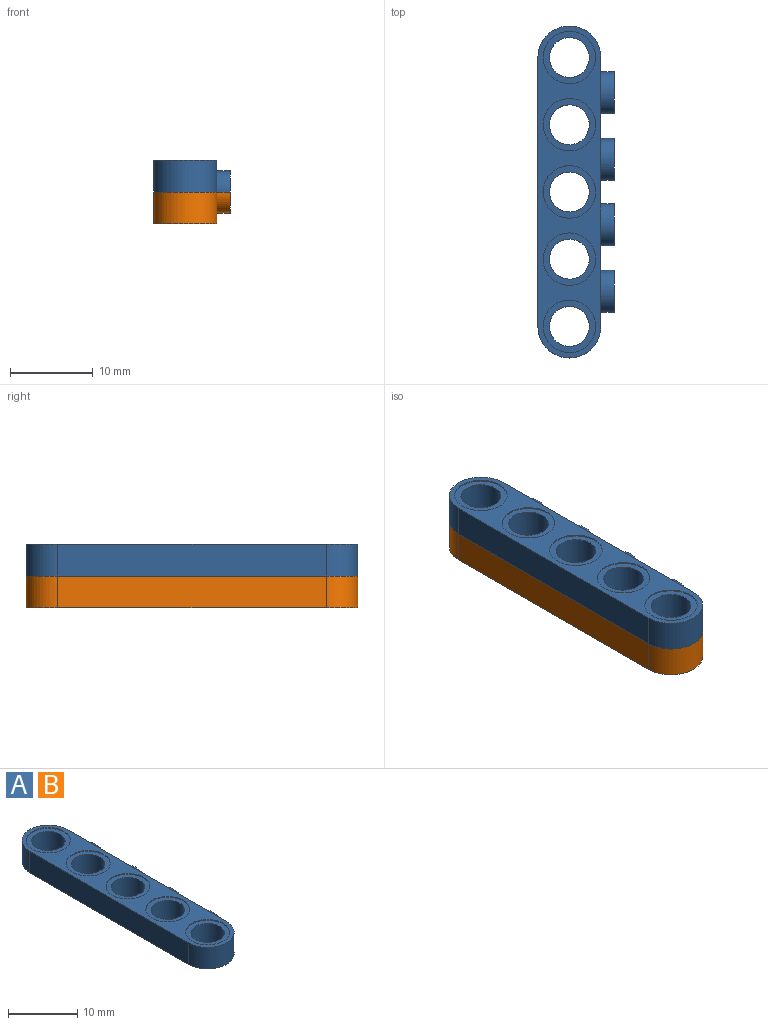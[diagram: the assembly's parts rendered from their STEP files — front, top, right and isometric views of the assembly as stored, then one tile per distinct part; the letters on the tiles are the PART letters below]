
ASSEMBLY  parts=2 mates=1
PART A: 37 faces, bbox 9.2x40.1x3.8 mm
  f0: plane 3.18x1.59mm, normal (1,0,0), area 4mm2, adj f14,f35
  f1: plane 3.18x1.59mm, normal (1,0,0), area 4mm2, adj f14,f32
  f2: plane 3.18x1.59mm, normal (1,0,0), area 4mm2, adj f14,f29
  f3: plane 3.18x1.59mm, normal (1,0,0), area 4mm2, adj f14,f26
  f4: plane 32.51x3.81mm, normal (-1,0,0), area 123.9mm2, adj f5,f11,f13,f14
  f5: cylinder r=3.81mm len=7.62mm, axis (0,0,-1), area 45.6mm2, adj f4,f6,f13,f14
  f6: plane 32.51x3.81mm, normal (1,0,0), area 83.3mm2, adj f5,f11,f13,f14,f25,f28,f31,f34
  f7: cylinder r=3.17mm len=6.35mm, axis (0,0,-1), area 2.5mm2, adj f13,f22
  f8: cylinder r=3.17mm len=6.35mm, axis (0,0,-1), area 2.5mm2, adj f13,f20
  f9: cylinder r=3.17mm len=6.35mm, axis (0,0,-1), area 2.5mm2, adj f13,f18
  f10: cylinder r=3.17mm len=6.35mm, axis (0,0,-1), area 2.5mm2, adj f13,f16
  f11: cylinder r=3.81mm len=7.62mm, axis (0,0,-1), area 45.6mm2, adj f4,f6,f13,f14
  f12: cylinder r=3.17mm len=6.35mm, axis (0,0,-1), area 2.5mm2, adj f13,f24
  f13: plane 40.13x7.62mm, normal (0,0,1), area 135mm2, adj f4,f5,f6,f7,f8,f9,f10,f11
  f14: plane 40.13x9.22mm, normal (0,0,-1), area 214.1mm2, adj f0,f1,f2,f3,f4,f5,f6,f11
  f15: cylinder r=2.41mm len=4.83mm, axis (0,0,-1), area 55.8mm2, adj f14,f16
  f16: plane 6.35x6.35mm, normal (0,0,1), area 13.4mm2, adj f10,f15
  f17: cylinder r=2.41mm len=4.83mm, axis (0,0,-1), area 55.8mm2, adj f14,f18
  f18: plane 6.35x6.35mm, normal (0,0,1), area 13.4mm2, adj f9,f17
  f19: cylinder r=2.41mm len=4.83mm, axis (0,0,-1), area 55.8mm2, adj f14,f20
  f20: plane 6.35x6.35mm, normal (0,0,1), area 13.4mm2, adj f8,f19
  f21: cylinder r=2.41mm len=4.83mm, axis (0,0,-1), area 55.8mm2, adj f14,f22
  f22: plane 6.35x6.35mm, normal (0,0,1), area 13.4mm2, adj f7,f21
  f23: cylinder r=2.41mm len=4.83mm, axis (0,0,-1), area 55.8mm2, adj f14,f24
  f24: plane 6.35x6.35mm, normal (0,0,1), area 13.4mm2, adj f12,f23
  f25: cylinder r=2.54mm len=5.08mm, axis (-1,0,0), area 12.8mm2, adj f6,f14,f27
  f26: cylinder r=1.59mm len=3.18mm, axis (-1,0,0), area 8mm2, adj f3,f14,f27
  f27: plane 5.08x2.54mm, normal (1,0,0), area 6.2mm2, adj f14,f25,f26
  f28: cylinder r=2.54mm len=5.08mm, axis (-1,0,0), area 12.8mm2, adj f6,f14,f30
  f29: cylinder r=1.59mm len=3.18mm, axis (-1,0,0), area 8mm2, adj f2,f14,f30
  f30: plane 5.08x2.54mm, normal (1,0,0), area 6.2mm2, adj f14,f28,f29
  f31: cylinder r=2.54mm len=5.08mm, axis (-1,0,0), area 12.8mm2, adj f6,f14,f33
  f32: cylinder r=1.59mm len=3.18mm, axis (-1,0,0), area 8mm2, adj f1,f14,f33
  f33: plane 5.08x2.54mm, normal (1,0,0), area 6.2mm2, adj f14,f31,f32
  f34: cylinder r=2.54mm len=5.08mm, axis (-1,0,0), area 12.8mm2, adj f6,f14,f36
  f35: cylinder r=1.59mm len=3.18mm, axis (-1,0,0), area 8mm2, adj f0,f14,f36
  f36: plane 5.08x2.54mm, normal (1,0,0), area 6.2mm2, adj f14,f34,f35
PART B: same geometry as A
PLACE A at identity
PLACE B rot(axis=(1,0,0),180deg) t=(0,-32.51,0)mm
MATE fastened B.f5 <-> A.f15  axis (0,0,1) through (0,0,0)mm
